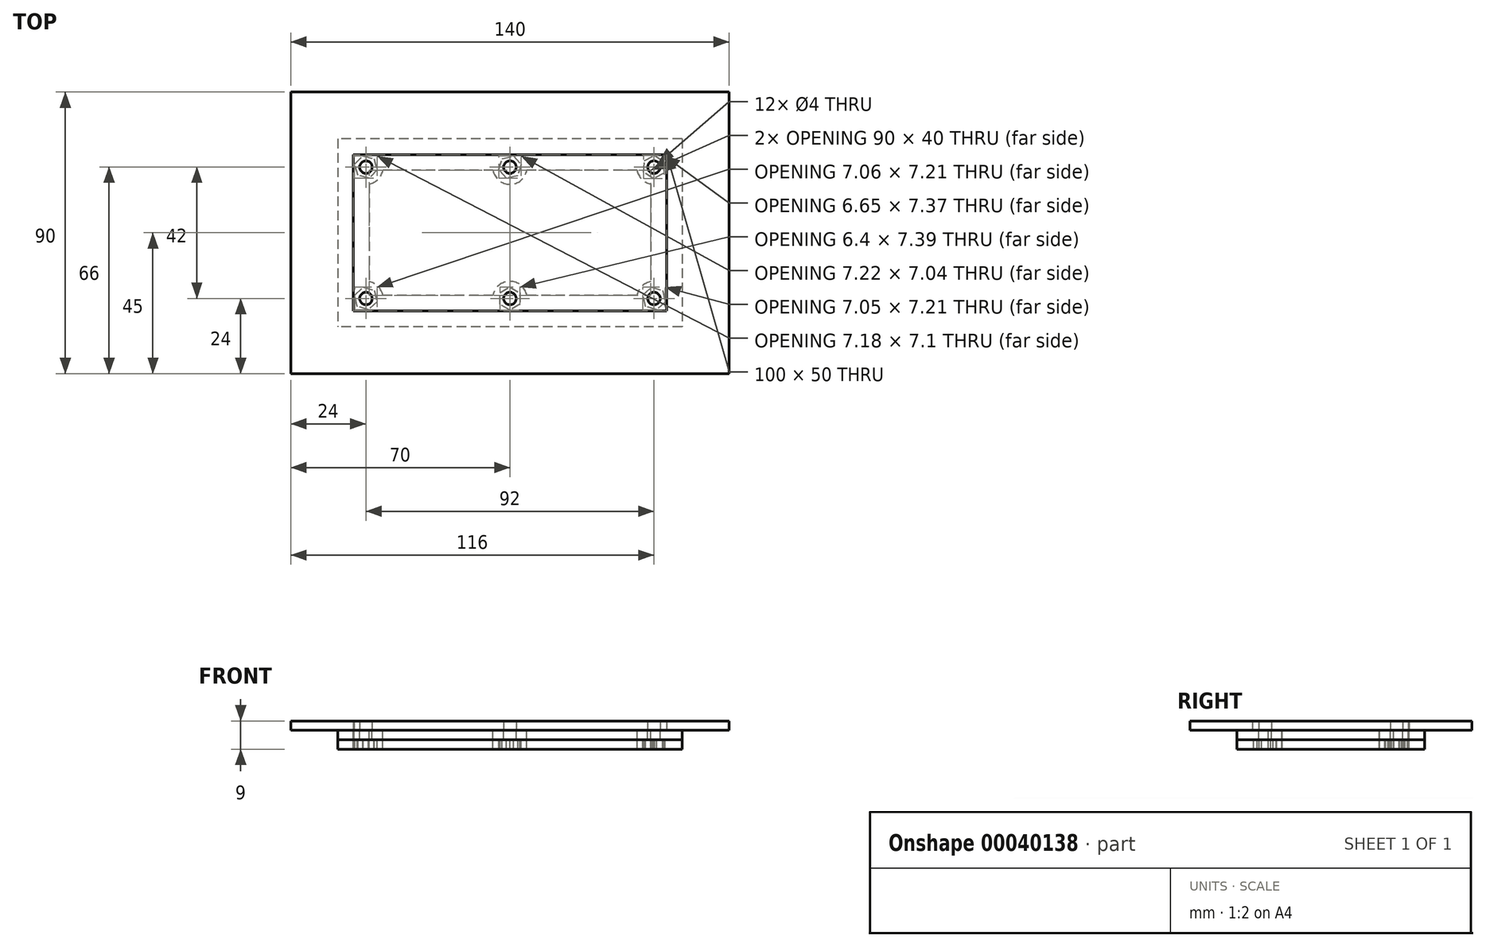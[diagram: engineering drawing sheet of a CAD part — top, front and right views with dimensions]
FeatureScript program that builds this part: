
annotation { "Feature Type Name" : "Feature", "Feature Type Description" : "" }
export const myFeature = defineFeature(function(context is Context, id is Id, definition is map)
    precondition{}
    {
        {
            var Q0;
            Q0=qCreatedBy(makeId("Top.planeOp"),FACE);
            var sketch = newSketch(context, id + "F0", { "sketchPlane" : qUnion([Q0])});
            skLineSegment(sketch, "E0.bottom", {"start": v(0, 0) * mm, "end": v(-100, 0) * mm});
            skLineSegment(sketch, "E0.top", {"start": v(0, -50) * mm, "end": v(-100, -50) * mm});
            skLineSegment(sketch, "E0.left", {"start": v(0, 0) * mm, "end": v(0, -50) * mm});
            skLineSegment(sketch, "E0.right", {"start": v(-100, 0) * mm, "end": v(-100, -50) * mm});
            skLineSegment(sketch, "E1.0", {"start": v(20, 20) * mm, "end": v(-120, 20) * mm});
            skLineSegment(sketch, "E1.1", {"start": v(20, 20) * mm, "end": v(20, -70) * mm});
            skLineSegment(sketch, "E1.2", {"start": v(20, -70) * mm, "end": v(-120, -70) * mm});
            skLineSegment(sketch, "E1.3", {"start": v(-120, 20) * mm, "end": v(-120, -70) * mm});
            skCircle(sketch, "E2", {"center": v(-96, -4) * mm, "radius": 2 * mm});
            skCircle(sketch, "E3", {"center": v(-96, -46) * mm, "radius": 2 * mm});
            skCircle(sketch, "E4", {"center": v(-4, -4) * mm, "radius": 2 * mm});
            skCircle(sketch, "E5", {"center": v(-4, -46) * mm, "radius": 2 * mm});
            skCircle(sketch, "E6", {"center": v(-50, -4) * mm, "radius": 2 * mm});
            skCircle(sketch, "E7", {"center": v(-50, -46) * mm, "radius": 2 * mm});
            skLineSegment(sketch, "E8.0", {"start": v(-9.4, -5) * mm, "end": v(-44.6, -5) * mm});
            skArc(sketch, "E9", {"start": v(-95, -9.4) * mm, "mid": v(-92.11, -7.89) * mm, "end": v(-90.6, -5) * mm});
            skArc(sketch, "E10", {"start": v(-90.6, -45) * mm, "mid": v(-92.11, -42.11) * mm, "end": v(-95, -40.6) * mm});
            skArc(sketch, "E11", {"start": v(-44.6, -45) * mm, "mid": v(-50, -40.5) * mm, "end": v(-55.4, -45) * mm});
            skArc(sketch, "E12", {"start": v(-55.4, -5) * mm, "mid": v(-50, -9.5) * mm, "end": v(-44.6, -5) * mm});
            skArc(sketch, "E13", {"start": v(-9.4, -5) * mm, "mid": v(-7.89, -7.89) * mm, "end": v(-5, -9.4) * mm});
            skArc(sketch, "E14", {"start": v(-5, -40.6) * mm, "mid": v(-7.89, -42.11) * mm, "end": v(-9.4, -45) * mm});
            skArc(sketch, "E15.trimOffspring", {"start": v(-99.77, 0) * mm, "mid": v(-99.89, -0.11) * mm, "end": v(-100, -0.23) * mm});
            skLineSegment(sketch, "E16.trimOffspring", {"start": v(-95, -9.4) * mm, "end": v(-95, -40.6) * mm});
            skLineSegment(sketch, "E17.trimOffspring", {"start": v(-55.4, -45) * mm, "end": v(-90.6, -45) * mm});
            skLineSegment(sketch, "E18.trimOffspring", {"start": v(-55.4, -5) * mm, "end": v(-90.6, -5) * mm});
            skLineSegment(sketch, "E19.trimOffspring", {"start": v(-5, -9.4) * mm, "end": v(-5, -40.6) * mm});
            skLineSegment(sketch, "E20.trimOffspring", {"start": v(-9.4, -45) * mm, "end": v(-44.6, -45) * mm});
            skLineSegment(sketch, "E21.0", {"start": v(5, -55) * mm, "end": v(-105, -55) * mm});
            skLineSegment(sketch, "E21.1", {"start": v(5, 5) * mm, "end": v(5, -55) * mm});
            skLineSegment(sketch, "E21.2", {"start": v(5, 5) * mm, "end": v(-105, 5) * mm});
            skLineSegment(sketch, "E21.3", {"start": v(-105, 5) * mm, "end": v(-105, -55) * mm});
            skCircle(sketch, "E22.cCircle", {"center": v(-96, -46) * mm, "radius": 3.2 * mm, "construction": true});
            skLineSegment(sketch, "E22.0", {"start": v(-96.81, -42.4) * mm, "end": v(-93.29, -43.5) * mm});
            skLineSegment(sketch, "E22.1", {"start": v(-93.29, -43.5) * mm, "end": v(-92.47, -47.1) * mm});
            skLineSegment(sketch, "E22.2", {"start": v(-92.47, -47.1) * mm, "end": v(-95.19, -49.6) * mm});
            skLineSegment(sketch, "E22.3", {"start": v(-95.19, -49.6) * mm, "end": v(-98.71, -48.5) * mm});
            skLineSegment(sketch, "E22.4", {"start": v(-98.71, -48.5) * mm, "end": v(-99.53, -44.9) * mm});
            skLineSegment(sketch, "E22.5", {"start": v(-99.53, -44.9) * mm, "end": v(-96.81, -42.4) * mm});
            skPoint(sketch, "E22.0.midPoint", {"position": v(-95.05, -42.94) * mm});
            skCircle(sketch, "E23.cCircle", {"center": v(-96, -4) * mm, "radius": 3.2 * mm, "construction": true});
            skLineSegment(sketch, "E23.0", {"start": v(-92.41, -4.88) * mm, "end": v(-94.97, -7.55) * mm});
            skLineSegment(sketch, "E23.1", {"start": v(-94.97, -7.55) * mm, "end": v(-98.56, -6.67) * mm});
            skLineSegment(sketch, "E23.2", {"start": v(-98.56, -6.67) * mm, "end": v(-99.59, -3.12) * mm});
            skLineSegment(sketch, "E23.3", {"start": v(-99.59, -3.12) * mm, "end": v(-97.03, -0.45) * mm});
            skLineSegment(sketch, "E23.4", {"start": v(-97.03, -0.45) * mm, "end": v(-93.44, -1.33) * mm});
            skLineSegment(sketch, "E23.5", {"start": v(-93.44, -1.33) * mm, "end": v(-92.41, -4.88) * mm});
            skPoint(sketch, "E23.0.midPoint", {"position": v(-93.7, -6.22) * mm});
            skCircle(sketch, "E24.cCircle", {"center": v(-4, -4) * mm, "radius": 3.2 * mm, "construction": true});
            skLineSegment(sketch, "E24.0", {"start": v(-0.94, -6.07) * mm, "end": v(-4.26, -7.69) * mm});
            skLineSegment(sketch, "E24.1", {"start": v(-4.26, -7.69) * mm, "end": v(-7.32, -5.61) * mm});
            skLineSegment(sketch, "E24.2", {"start": v(-7.32, -5.61) * mm, "end": v(-7.06, -1.93) * mm});
            skLineSegment(sketch, "E24.3", {"start": v(-7.06, -1.93) * mm, "end": v(-3.74, -0.31) * mm});
            skLineSegment(sketch, "E24.4", {"start": v(-3.74, -0.31) * mm, "end": v(-0.68, -2.39) * mm});
            skLineSegment(sketch, "E24.5", {"start": v(-0.68, -2.39) * mm, "end": v(-0.94, -6.07) * mm});
            skPoint(sketch, "E24.0.midPoint", {"position": v(-2.6, -6.88) * mm});
            skCircle(sketch, "E25.cCircle", {"center": v(-4, -46) * mm, "radius": 3.2 * mm, "construction": true});
            skLineSegment(sketch, "E25.0", {"start": v(-7.53, -44.9) * mm, "end": v(-4.8, -42.4) * mm});
            skLineSegment(sketch, "E25.1", {"start": v(-4.8, -42.4) * mm, "end": v(-1.28, -43.5) * mm});
            skLineSegment(sketch, "E25.2", {"start": v(-1.28, -43.5) * mm, "end": v(-0.47, -47.1) * mm});
            skLineSegment(sketch, "E25.3", {"start": v(-0.47, -47.1) * mm, "end": v(-3.2, -49.6) * mm});
            skLineSegment(sketch, "E25.4", {"start": v(-3.2, -49.6) * mm, "end": v(-6.72, -48.5) * mm});
            skLineSegment(sketch, "E25.5", {"start": v(-6.72, -48.5) * mm, "end": v(-7.53, -44.9) * mm});
            skPoint(sketch, "E25.0.midPoint", {"position": v(-6.17, -43.64) * mm});
            skCircle(sketch, "E26.cCircle", {"center": v(-50, -46) * mm, "radius": 3.2 * mm, "construction": true});
            skLineSegment(sketch, "E26.0", {"start": v(-46.8, -44.15) * mm, "end": v(-46.8, -47.85) * mm});
            skLineSegment(sketch, "E26.1", {"start": v(-46.8, -47.85) * mm, "end": v(-50, -49.7) * mm});
            skLineSegment(sketch, "E26.2", {"start": v(-50, -49.7) * mm, "end": v(-53.2, -47.85) * mm});
            skLineSegment(sketch, "E26.3", {"start": v(-53.2, -47.85) * mm, "end": v(-53.2, -44.15) * mm});
            skLineSegment(sketch, "E26.4", {"start": v(-53.2, -44.15) * mm, "end": v(-50, -42.3) * mm});
            skLineSegment(sketch, "E26.5", {"start": v(-50, -42.3) * mm, "end": v(-46.8, -44.15) * mm});
            skPoint(sketch, "E26.0.midPoint", {"position": v(-46.8, -46) * mm});
            skCircle(sketch, "E27.cCircle", {"center": v(-50, -4) * mm, "radius": 3.2 * mm, "construction": true});
            skLineSegment(sketch, "E27.0", {"start": v(-47.5, -6.73) * mm, "end": v(-51.12, -7.52) * mm});
            skLineSegment(sketch, "E27.1", {"start": v(-51.12, -7.52) * mm, "end": v(-53.6, -4.8) * mm});
            skLineSegment(sketch, "E27.2", {"start": v(-53.6, -4.8) * mm, "end": v(-52.5, -1.27) * mm});
            skLineSegment(sketch, "E27.3", {"start": v(-52.5, -1.27) * mm, "end": v(-48.88, -0.48) * mm});
            skLineSegment(sketch, "E27.4", {"start": v(-48.88, -0.48) * mm, "end": v(-46.4, -3.2) * mm});
            skLineSegment(sketch, "E27.5", {"start": v(-46.4, -3.2) * mm, "end": v(-47.5, -6.73) * mm});
            skPoint(sketch, "E27.0.midPoint", {"position": v(-49.31, -7.13) * mm});
            skSolve(sketch);
        }
        {
            var Q0;
            Q0=makeQuery(id+"F0.imprint","IMPRINT",FACE,{"disambiguationData":[TD([[makeQuery(id+"F0.imprint","IMPRINT",EDGE,{"derivedFrom":sQuery(id+"F0.wireOp",EDGE,"E1.0")}),1.0]])]});
            var Q1;
            {var subQ3=sQuery(id+"F0.wireOp",EDGE,"E0.top");Q1=makeQuery(id+"F0.imprint","IMPRINT",FACE,{"disambiguationData":[TD([[makeQuery(id+"F0.imprint","IMPRINT",EDGE,{"derivedFrom":subQ3}),1.0]])]});}
            extrude(context, id + "F1", {"entities" : qUnion([Q0, Q1]), "depth" : 3 * mm});
        }
        {
            var Q0;
            {var subQ3=sQuery(id+"F0.wireOp",EDGE,"E0.top");Q0=makeQuery(id+"F0.imprint","IMPRINT",FACE,{"disambiguationData":[TD([[makeQuery(id+"F0.imprint","IMPRINT",EDGE,{"derivedFrom":subQ3}),1.0]])]});}
            var Q1;
            {var subQ0=sQuery(id+"F0.wireOp",EDGE,"E0.top");Q1=makeQuery(id+"F0.imprint","IMPRINT",FACE,{"disambiguationData":[TD([[makeQuery(id+"F0.imprint","IMPRINT",EDGE,{"derivedFrom":subQ0}),-1.0]])]});}
            var Q2;
            Q2=makeQuery(id+"F0.imprint","IMPRINT",FACE,{"disambiguationData":[TD([[makeQuery(id+"F0.imprint","IMPRINT",EDGE,{"derivedFrom":sQuery(id+"F0.wireOp",EDGE,"E3")}),-1.0]])]});
            var Q3;
            Q3=makeQuery(id+"F0.imprint","IMPRINT",FACE,{"disambiguationData":[TD([[makeQuery(id+"F0.imprint","IMPRINT",EDGE,{"derivedFrom":sQuery(id+"F0.wireOp",EDGE,"E2")}),-1.0]])]});
            var Q4;
            Q4=makeQuery(id+"F0.imprint","IMPRINT",FACE,{"disambiguationData":[TD([[makeQuery(id+"F0.imprint","IMPRINT",EDGE,{"derivedFrom":sQuery(id+"F0.wireOp",EDGE,"E7")}),-1.0]])]});
            var Q5;
            Q5=makeQuery(id+"F0.imprint","IMPRINT",FACE,{"disambiguationData":[TD([[makeQuery(id+"F0.imprint","IMPRINT",EDGE,{"derivedFrom":sQuery(id+"F0.wireOp",EDGE,"E6")}),-1.0]])]});
            var Q6;
            Q6=makeQuery(id+"F0.imprint","IMPRINT",FACE,{"disambiguationData":[TD([[makeQuery(id+"F0.imprint","IMPRINT",EDGE,{"derivedFrom":sQuery(id+"F0.wireOp",EDGE,"E4")}),-1.0]])]});
            var Q7;
            Q7=makeQuery(id+"F0.imprint","IMPRINT",FACE,{"disambiguationData":[TD([[makeQuery(id+"F0.imprint","IMPRINT",EDGE,{"derivedFrom":sQuery(id+"F0.wireOp",EDGE,"E5")}),-1.0]])]});
            extrude(context, id + "F2", {"entities" : qUnion([Q0, Q1, Q2, Q3, Q4, Q5, Q6, Q7]), "oppositeDirection" : true, "depth" : 3 * mm});
        }
        {
            var Q0;
            {var subQ0=sQuery(id+"F0.wireOp",EDGE,"E0.top");Q0=makeQuery(id+"F0.imprint","IMPRINT",FACE,{"disambiguationData":[TD([[makeQuery(id+"F0.imprint","IMPRINT",EDGE,{"derivedFrom":subQ0}),-1.0]])]});}
            var Q1;
            Q1=makeQuery(id+"F0.imprint","IMPRINT",FACE,{"disambiguationData":[TD([[makeQuery(id+"F0.imprint","IMPRINT",EDGE,{"derivedFrom":sQuery(id+"F0.wireOp",EDGE,"E8.0")}),1.0]])]});
            var Q2;
            Q2=makeQuery(id+"F0.imprint","IMPRINT",FACE,{"disambiguationData":[TD([[makeQuery(id+"F0.imprint","IMPRINT",EDGE,{"derivedFrom":sQuery(id+"F0.wireOp",EDGE,"E2")}),-1.0]])]});
            var Q3;
            Q3=makeQuery(id+"F0.imprint","IMPRINT",FACE,{"disambiguationData":[TD([[makeQuery(id+"F0.imprint","IMPRINT",EDGE,{"derivedFrom":sQuery(id+"F0.wireOp",EDGE,"E3")}),-1.0]])]});
            var Q4;
            Q4=makeQuery(id+"F0.imprint","IMPRINT",FACE,{"disambiguationData":[TD([[makeQuery(id+"F0.imprint","IMPRINT",EDGE,{"derivedFrom":sQuery(id+"F0.wireOp",EDGE,"E6")}),-1.0]])]});
            var Q5;
            Q5=makeQuery(id+"F0.imprint","IMPRINT",FACE,{"disambiguationData":[TD([[makeQuery(id+"F0.imprint","IMPRINT",EDGE,{"derivedFrom":sQuery(id+"F0.wireOp",EDGE,"E7")}),-1.0]])]});
            var Q6;
            Q6=makeQuery(id+"F0.imprint","IMPRINT",FACE,{"disambiguationData":[TD([[makeQuery(id+"F0.imprint","IMPRINT",EDGE,{"derivedFrom":sQuery(id+"F0.wireOp",EDGE,"E4")}),-1.0]])]});
            var Q7;
            Q7=makeQuery(id+"F0.imprint","IMPRINT",FACE,{"disambiguationData":[TD([[makeQuery(id+"F0.imprint","IMPRINT",EDGE,{"derivedFrom":sQuery(id+"F0.wireOp",EDGE,"E5")}),-1.0]])]});
            extrude(context, id + "F3", {"entities" : qUnion([Q0, Q1, Q2, Q3, Q4, Q5, Q6, Q7]), "depth" : 3 * mm});
        }
        {
            var Q0;
            {var subQ0=sQuery(id+"F0.wireOp",EDGE,"E0.top");Q0=makeQuery(id+"F0.imprint","IMPRINT",FACE,{"disambiguationData":[TD([[makeQuery(id+"F0.imprint","IMPRINT",EDGE,{"derivedFrom":subQ0}),-1.0]])]});}
            var Q1;
            {var subQ3=sQuery(id+"F0.wireOp",EDGE,"E0.top");Q1=makeQuery(id+"F0.imprint","IMPRINT",FACE,{"disambiguationData":[TD([[makeQuery(id+"F0.imprint","IMPRINT",EDGE,{"derivedFrom":subQ3}),1.0]])]});}
            extrude(context, id + "F4", {"entities" : qUnion([Q0, Q1]), "oppositeDirection" : true, "depth" : 6 * mm, "hasSecondDirection" : true, "secondDirectionOppositeDirection" : true, "secondDirectionDepth" : 3 * mm});
        }
    });
